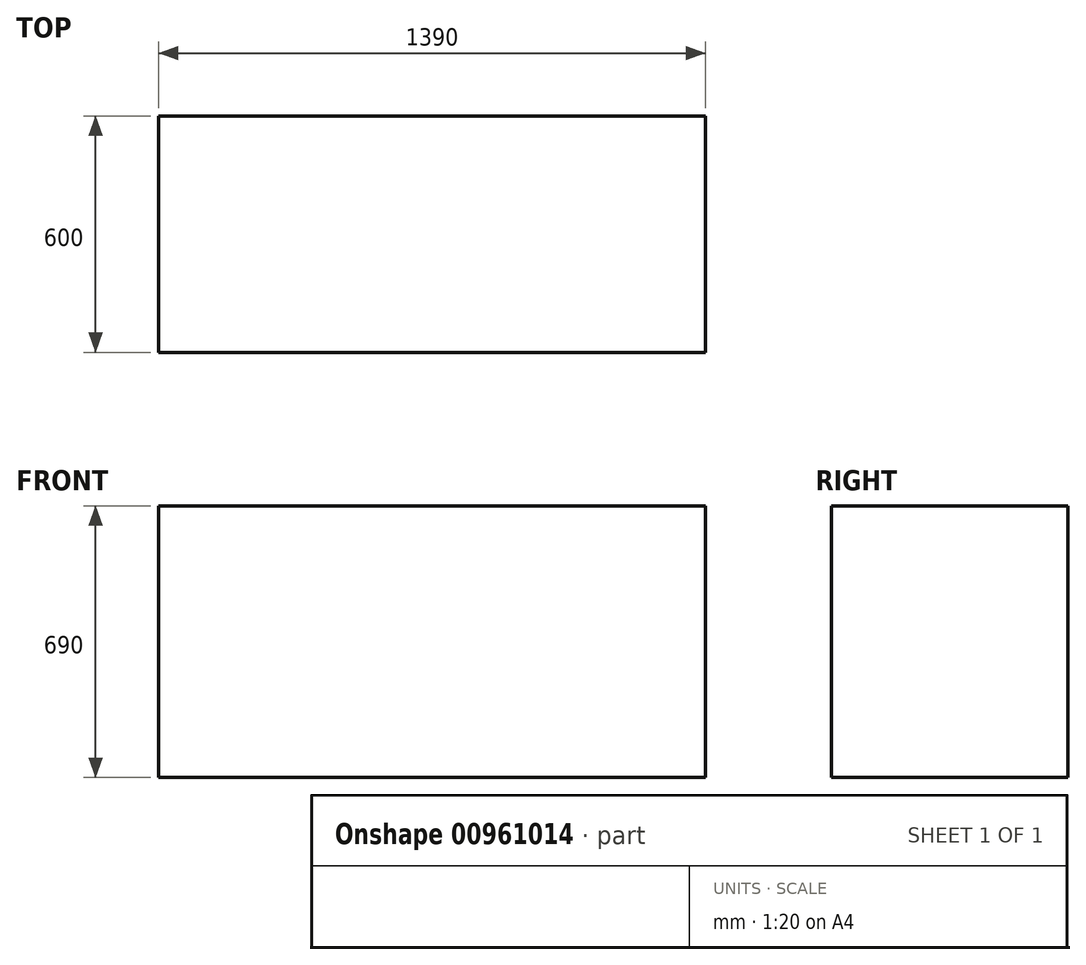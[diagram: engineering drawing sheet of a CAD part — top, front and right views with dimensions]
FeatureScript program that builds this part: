
annotation { "Feature Type Name" : "Feature", "Feature Type Description" : "" }
export const myFeature = defineFeature(function(context is Context, id is Id, definition is map)
    precondition{}
    {
        {
            var Q0;
            Q0=qCreatedBy(makeId("Front.planeOp"),FACE);
            var sketch = newSketch(context, id + "F0", { "sketchPlane" : qUnion([Q0])});
            skLineSegment(sketch, "E0.bottom", {"start": v(-1257, 690) * mm, "end": v(133, 690) * mm});
            skLineSegment(sketch, "E0.top", {"start": v(-1257, 0) * mm, "end": v(133, 0) * mm});
            skLineSegment(sketch, "E0.left", {"start": v(-1257, 690) * mm, "end": v(-1257, 0) * mm});
            skLineSegment(sketch, "E0.right", {"start": v(133, 690) * mm, "end": v(133, 0) * mm});
            skSolve(sketch);
        }
        {
            var Q0;
            Q0=makeQuery(id+"F0.imprint","IMPRINT",FACE,{"disambiguationData":[TD([[makeQuery(id+"F0.imprint","IMPRINT",EDGE,{"derivedFrom":sQuery(id+"F0.wireOp",EDGE,"E0.bottom")}),-1.0]])]});
            extrude(context, id + "F1", {"entities" : qUnion([Q0]), "depth" : 600 * mm, "offsetDistance" : 25 * mm});
        }
    });
